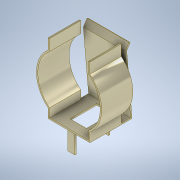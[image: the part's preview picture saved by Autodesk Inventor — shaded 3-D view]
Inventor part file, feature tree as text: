
AUTODESK INVENTOR PART (.ipt)
format: ipt  version: 2022 (Build 260153000, 153)  size: 203,264 bytes
history: native  units: mm
features: extrude x7, sketch x7, other x4
ambient origin geometry x8: Origin, YZ Plane, XZ Plane, XY Plane, X Axis, Y Axis, Z Axis, Center Point
bodies: Body1 (feature_tree)
feature tree (18):
  other  "ソリッド1"
  extrude  "押し出し1"  Depth=9.0mm
  extrude  "押し出し2"  Depth=2.0mm
  other  "作業平面1"
  extrude  "押し出し3"  Depth=14.0mm
  other  "作業平面2"
  extrude  "押し出し4"  Depth=0.3mm
  extrude  "押し出し5"  Depth=0.3mm
  extrude  "押し出し7"  Depth=0.3mm
  other  "作業平面3"
  extrude  "押し出し8"  Depth=15.0mm
  sketch  "スケッチ1"
  sketch  "スケッチ2"
  sketch  "スケッチ3"
  sketch  "スケッチ4"
  sketch  "スケッチ5"
  sketch  "スケッチ7"
  sketch  "スケッチ8"
